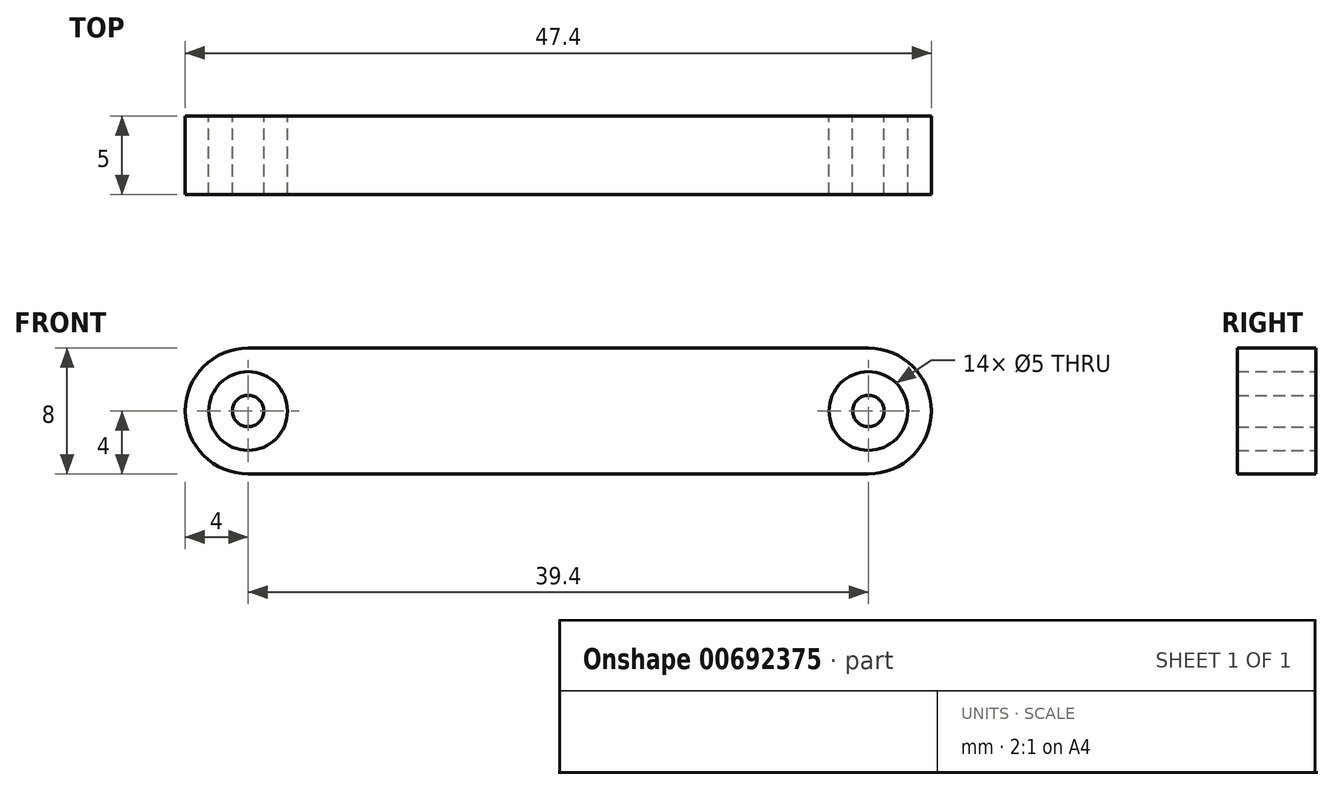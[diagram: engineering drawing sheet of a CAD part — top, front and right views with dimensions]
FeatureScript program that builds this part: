
annotation { "Feature Type Name" : "Feature", "Feature Type Description" : "" }
export const myFeature = defineFeature(function(context is Context, id is Id, definition is map)
    precondition{}
    {
        {
            var Q0;
            Q0=qCreatedBy(makeId("Front.planeOp"),FACE);
            var sketch = newSketch(context, id + "F0", { "sketchPlane" : qUnion([Q0])});
            skArc(sketch, "E0", {"start": v(0, 4) * mm, "mid": v(-4, 0) * mm, "end": v(0, -4) * mm});
            skArc(sketch, "E1", {"start": v(39.4, -4) * mm, "mid": v(43.4, 0) * mm, "end": v(39.4, 4) * mm});
            skLineSegment(sketch, "E2", {"start": v(0, 4) * mm, "end": v(39.4, 4) * mm});
            skLineSegment(sketch, "E3", {"start": v(0, -4) * mm, "end": v(39.4, -4) * mm});
            skCircle(sketch, "E4", {"center": v(0, 0) * mm, "radius": 2.5 * mm});
            skCircle(sketch, "E5", {"center": v(39.4, 0) * mm, "radius": 2.5 * mm});
            skCircle(sketch, "E6", {"center": v(39.4, 0) * mm, "radius": 1 * mm});
            skCircle(sketch, "E7", {"center": v(0, 0) * mm, "radius": 1 * mm});
            skSolve(sketch);
        }
        {
            var Q0;
            Q0 = qSketchRegion(id + "F0", true);
            var Q1;
            Q1=makeQuery(id+"F0.imprint","IMPRINT",FACE,{"disambiguationData":[TD([[makeQuery(id+"F0.imprint","IMPRINT",EDGE,{"derivedFrom":sQuery(id+"F0.wireOp",EDGE,"E7")}),1.0]])]});
            var Q2;
            Q2=makeQuery(id+"F0.imprint","IMPRINT",FACE,{"disambiguationData":[TD([[makeQuery(id+"F0.imprint","IMPRINT",EDGE,{"derivedFrom":sQuery(id+"F0.wireOp",EDGE,"E6")}),1.0]])]});
            extrude(context, id + "F1", {"entities" : qUnion([Q0, Q1, Q2]), "depth" : 5 * mm, "offsetDistance" : 25 * mm});
        }
    });
